# Revit family: PlumbingFixture_Tap_Galvin_TC50
name_source: partatom
category: Plumbing Fixtures
revit_build: Autodesk Revit MEP 2012 (Build: 20110916_2132(x64)
units: mm (PartAtom-declared; Revit-internal decimal feet)

## types (4) — shared parameters
Assembly Code = D2010
Circulation_ANZRS = Yes
Description = CliniLever® CP Hob Mixing Set
FilterObject_ANZRS = TL50
FlowRate = 0.1166 L/s
Inlet = 15mm Male
Instructions = http://www.galvinengineering.com.au
Keynote = 10800
Manufacturer = Galvin Engineering
ModifiedIssue_ANZRS = 20140526 $
PlumbingFinish = Chrome
PlumbingMaterial_ANZRS = Metal_Taps_DR-Brass-with-Chrome-Finish_10800
StyleOrType_ANZRS = Plumbing Fixture
Type Comments = TL50
URL = www.galvinengineering.com.au
WELSRating_ANZRS = 4 star
zero-valued in all types: Default Elevation

## per-type parameters (varying)
| type | Outlet | Seating |
| TC50FC1C | Fixed Spout | Ceramic Disc |
| TC50FJ1C | Fixed Spout | Jumper Valve |
| TC50SC1C | Swivel Spout | Ceramic Disc |
| TC50SJ1C | Swivel Spout | Jumper Valve |

note: column(s) folded — value = type name in every type: Model

## geometry (parser evidence)
native form markers: Blend x1, Sweep x1
no freeform markers — native parametric forms only
